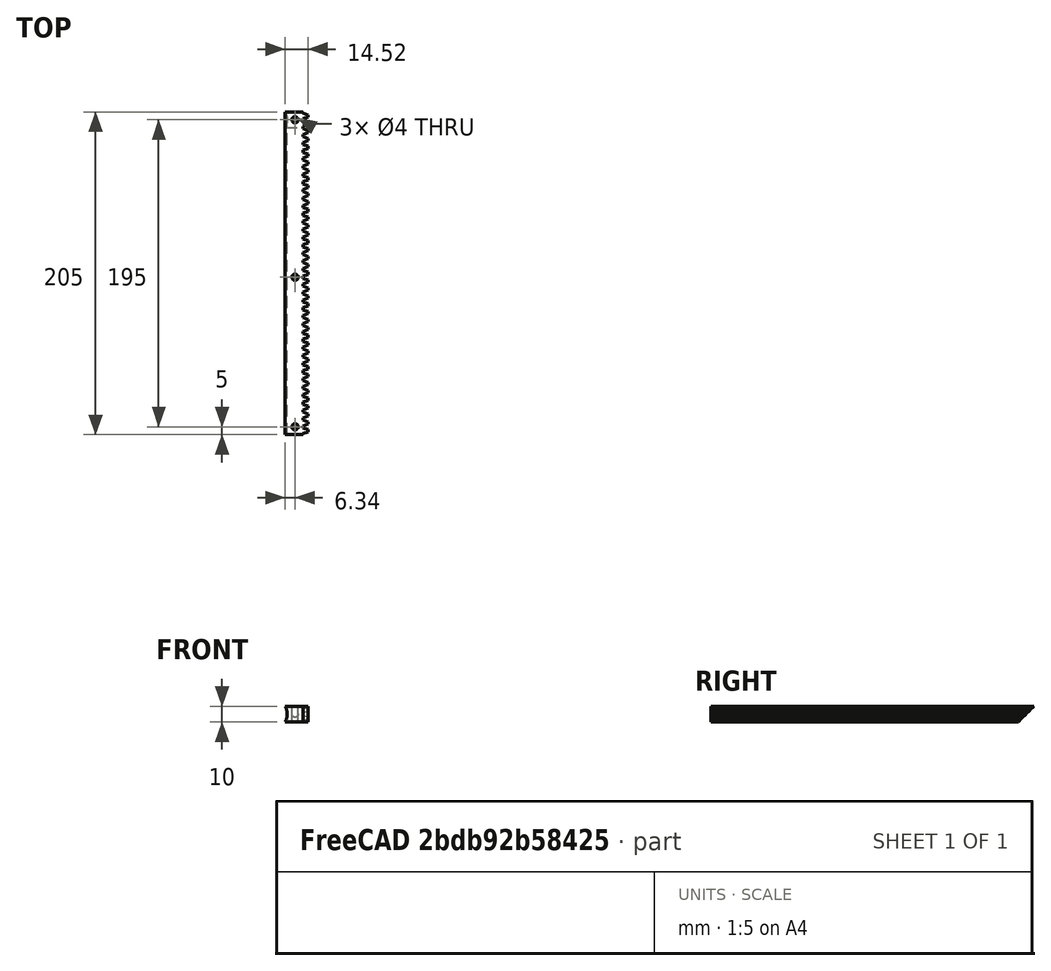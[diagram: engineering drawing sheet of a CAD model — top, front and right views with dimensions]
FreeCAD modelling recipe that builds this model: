
FCSTD DOCUMENT  (FreeCAD 0.17R13522 (Git))
Label: rack-end
License: All rights reserved
LicenseURL: http://en.wikipedia.org/wiki/All_rights_reserved
objects: Part::Cylinder×4, Part::Box×2, Part::MultiFuse×2, Part::FeaturePython×1, Part::Cut×1
note: 10 computed .brp shape members not serialized (recipe doc carries the construction recipe); baked Part::Feature solids carry a one-line shape summary decoded from their .brp

FEATURE [Part::FeaturePython] InvoluteRack  # WARN: FeaturePython — macro-defined, semantics opaque (R4)
  Placement = pos=(11.5915,2.5,-5) rot=(0,0,1;0rad)
  beta = 0
  double_helix = false
  head = 0
  height = 10
  module = 1.59155
  pressure_angle = 20
  teeth = 41
  thickness = 1
  expr: Placement.Base.x = 10 + 5 / pi
  expr: module = 5 / pi
FEATURE [Part::Box] Box  label="Cube"
  AttacherType = Attacher::AttachEngine3D
  Height = 10
  Length = 12
  Placement = pos=(-2,0,-5) rot=(0,0,1;0rad)
  Width = 205
FEATURE [Part::Cylinder] Cylinder
  Angle = 360
  AttacherType = Attacher::AttachEngine3D
  Height = 10
  Placement = pos=(5,5,-5) rot=(0,0,1;0rad)
  Radius = 2
FEATURE [Part::Cylinder] Cylinder001
  Angle = 360
  AttacherType = Attacher::AttachEngine3D
  Height = 10
  Placement = pos=(5,100,-5) rot=(0,0,1;0rad)
  Radius = 2
FEATURE [Part::Cylinder] Cylinder002
  Angle = 360
  AttacherType = Attacher::AttachEngine3D
  Height = 10
  Placement = pos=(5,200,-5) rot=(0,0,1;0rad)
  Radius = 2
FEATURE [Part::MultiFuse] Fusion  label="Positive Fusion"
  Shapes = -> [Box,InvoluteRack]
FEATURE [Part::Cylinder] Cylinder003  label="Rail"
  Angle = 360
  AttacherType = Attacher::AttachEngine3D
  Height = 210
  Placement = pos=(-10,0,0) rot=(-1,0,0;1.5708rad)
  Radius = 10
FEATURE [Part::Box] Box002  label="Cube002"
  AttacherType = Attacher::AttachEngine3D
  Height = 20
  Length = 20
  Placement = pos=(-5,195,-5) rot=(-1,0,0;0.785398rad)
  Width = 10
FEATURE [Part::MultiFuse] Fusion001  label="Negative Fusion"
  Shapes = -> [Cylinder,Cylinder001,Cylinder002,Cylinder003,Box002]
FEATURE [Part::Cut] Cut
  Base = -> Fusion
  Tool = -> Fusion001
